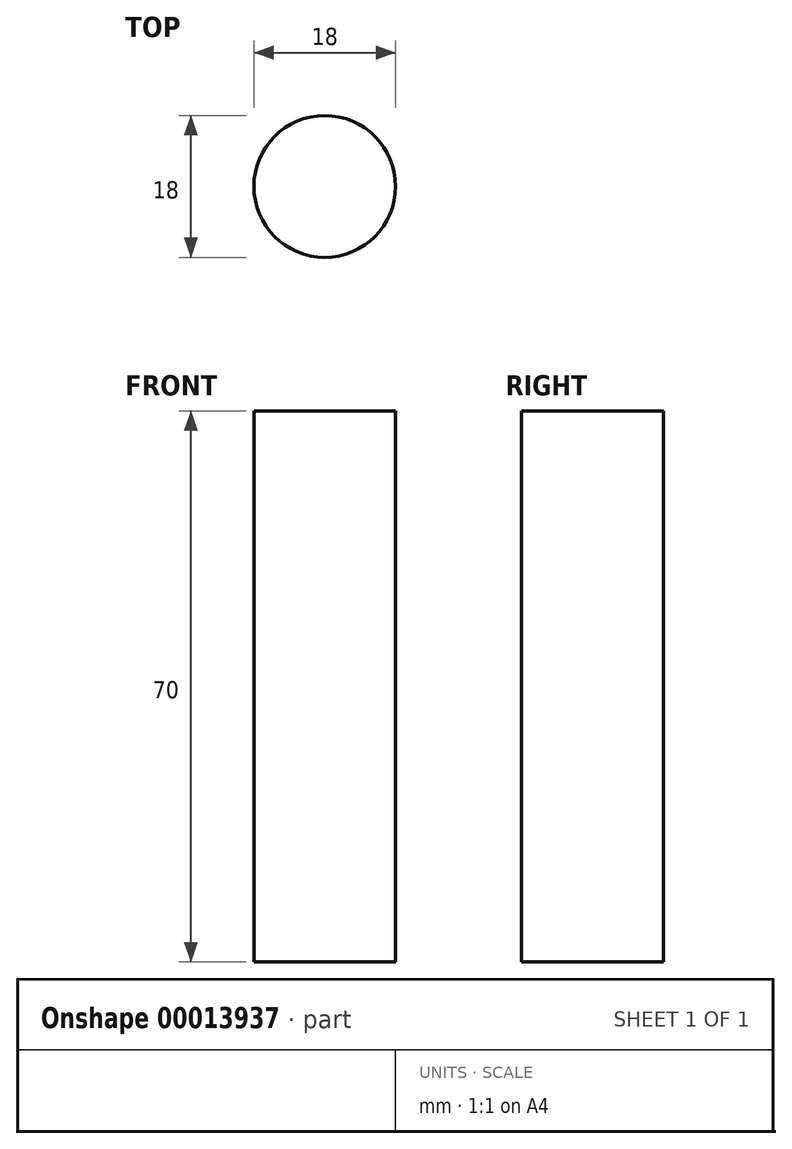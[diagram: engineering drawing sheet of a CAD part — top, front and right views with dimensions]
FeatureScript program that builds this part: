
annotation { "Feature Type Name" : "Feature", "Feature Type Description" : "" }
export const myFeature = defineFeature(function(context is Context, id is Id, definition is map)
    precondition{}
    {
        {
            var Q0;
            Q0=qCreatedBy(makeId("Top.planeOp"),FACE);
            var sketch = newSketch(context, id + "F0", { "sketchPlane" : qUnion([Q0])});
            skCircle(sketch, "E0", {"center": v(0, 0) * mm, "radius": 9 * mm});
            skSolve(sketch);
        }
        {
            var Q0;
            Q0=makeQuery(id+"F0.imprint","IMPRINT",FACE,{"disambiguationData":[TD([[makeQuery(id+"F0.imprint","IMPRINT",EDGE,{"derivedFrom":sQuery(id+"F0.wireOp",EDGE,"E0")}),1.0]])]});
            extrude(context, id + "F1", {"entities" : qUnion([Q0]), "depth" : 70 * mm});
        }
    });
